# Revit family: LA2-X
name_source: partatom
category: Lighting Fixtures
revit_build: Autodesk Revit 2014 (Build: 20130709_2115(x64)
units: mm (PartAtom-declared; Revit-internal decimal feet)

## types (3) — shared parameters
Color Filter = 16777215
Comments = This model is for use in spatial massing and rendering. Please contact LightArt for pick-point placement and installation details.
Description = L - 36w, 700mA, 2900 lumens
Diffuser = White Opal Acrylic
Dimming Compatibility = 0-10v
Dimming Lamp Color Temperature Shift = <None>
Driver = 24v
Emit Shape Visible in Rendering = No
Emit from Circle Diameter = 2' - 0"
Hardware = Stainless Steel Cables
Height From Ceiling = 2' - 0"
Input = 120v-277v
LIGHTING = Solid State LED System
120v-277v input; 24v driver;
0-10v dimming compatible
3000k 81 CRI light source
S - 14w, 1050mA, 1045 lumens
Light Source Symbol Size = 1' - 6"
Manufacturer = LightArt
Model = LA2-X
STANDARDS = 3-6 week lead time, UL Compliant / CSA Approved, Damp Rated
Shade = 3form Varia Ecoresin
Type Comments = Stainless steel canopy mounts to
standard junction box (provided by others)

## per-type parameters (varying)
| type | HARDWARE_2 | Height | Weight |
| X - 42"x 4" | Removable powder coated lid | 0' - 4" | 20 lbs |
| X - 42"x 8" | Removable powder coated lid
Stainless steel canopy mounts to
standard junction box (provided by others)
(3-4) 3/64” stainless steel cables to canopy
Silver power cord to canopy
Adjustable 24”-96” suspension | 0' - 8" | 21lbs |
| X - 42" x12" | Removable powder coated lid | 1' - 0" | 22 lbs |

## geometry (parser evidence)
native form markers: Blend x2, Sweep x12
no freeform markers — native parametric forms only
